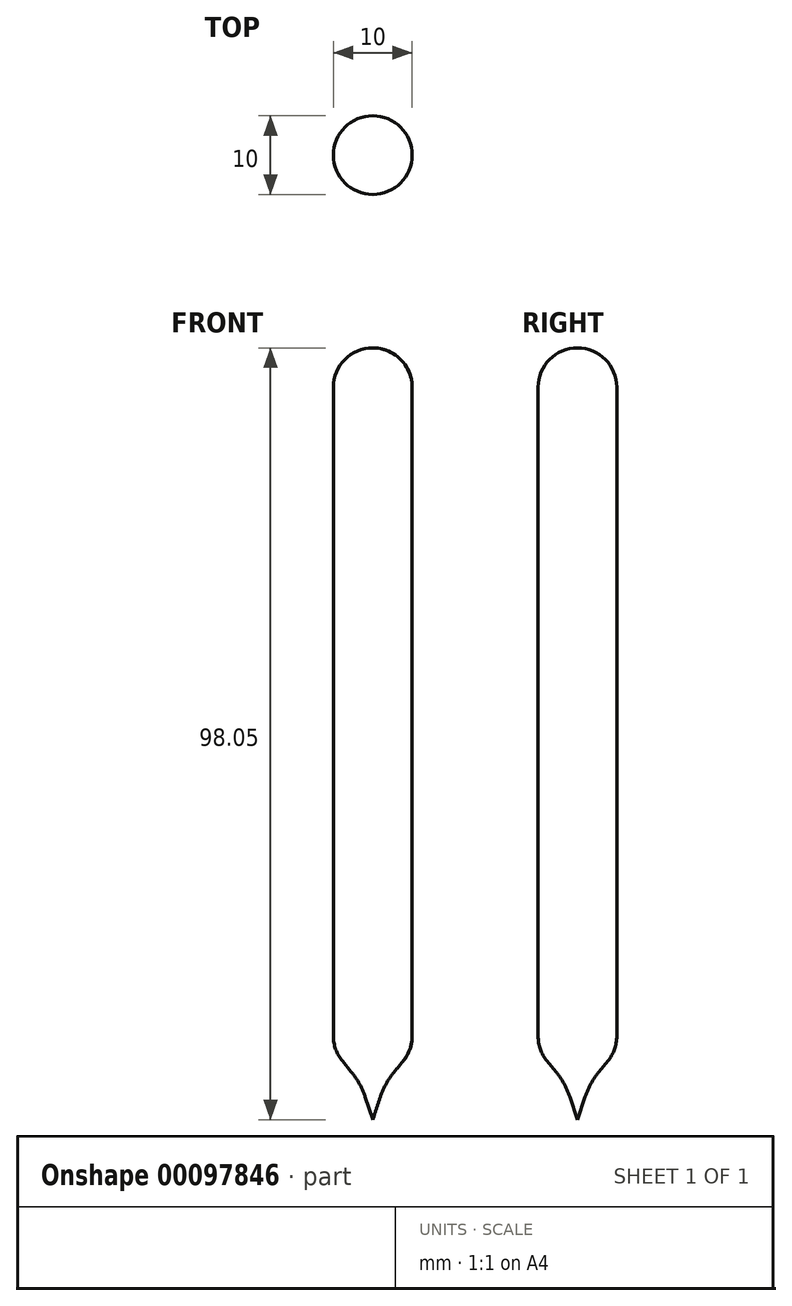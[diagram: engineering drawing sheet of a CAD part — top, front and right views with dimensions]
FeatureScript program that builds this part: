
annotation { "Feature Type Name" : "Feature", "Feature Type Description" : "" }
export const myFeature = defineFeature(function(context is Context, id is Id, definition is map)
    precondition{}
    {
        {
            var Q0;
            Q0=qCreatedBy(makeId("Front.planeOp"),FACE);
            var sketch = newSketch(context, id + "F0", { "sketchPlane" : qUnion([Q0])});
            skLineSegment(sketch, "E0", {"start": v(0, 55.8) * mm, "end": v(0, 55.8) * mm});
            skLineSegment(sketch, "E1", {"start": v(5, 50.8) * mm, "end": v(5, -31.63) * mm});
            skLineSegment(sketch, "E2", {"start": v(3.86, -34.8) * mm, "end": v(2.73, -36.17) * mm});
            skLineSegment(sketch, "E3", {"start": v(0.96, -39.37) * mm, "end": v(0, -42.26) * mm});
            skPoint(sketch, "E4.visualSharp", {"position": v(5, 55.8) * mm});
            skArc(sketch, "E4.filletArc", {"start": v(5, 50.8) * mm, "mid": v(3.54, 54.33) * mm, "end": v(0, 55.8) * mm});
            skPoint(sketch, "E5.visualSharp", {"position": v(5, -33.42) * mm});
            skArc(sketch, "E5.filletArc", {"start": v(3.86, -34.8) * mm, "mid": v(4.7, -33.32) * mm, "end": v(5, -31.63) * mm});
            skPoint(sketch, "E6.visualSharp", {"position": v(1.55, -37.6) * mm});
            skArc(sketch, "E6.filletArc", {"start": v(2.73, -36.17) * mm, "mid": v(1.7, -37.69) * mm, "end": v(0.96, -39.37) * mm});
            skLineSegment(sketch, "E7", {"start": v(0, 0) * mm, "end": v(5, 0) * mm, "construction": true});
            skLineSegment(sketch, "E8", {"start": v(0, 55.8) * mm, "end": v(0, -42.26) * mm});
            skSolve(sketch);
        }
        {
            var Q0;
            Q0=makeQuery(id+"F0.imprint","IMPRINT",FACE,{"disambiguationData":[TD([[makeQuery(id+"F0.imprint","IMPRINT",EDGE,{"derivedFrom":sQuery(id+"F0.wireOp",EDGE,"E1")}),-1.0]])]});
            var Q1;
            Q1=sQuery(id+"F0.wireOp",EDGE,"E8");
            revolve(context, id + "F1", {"entities" : qUnion([Q0]), "axis" : qUnion([Q1]), "revolveType" : RevolveType.FULL});
        }
    });
